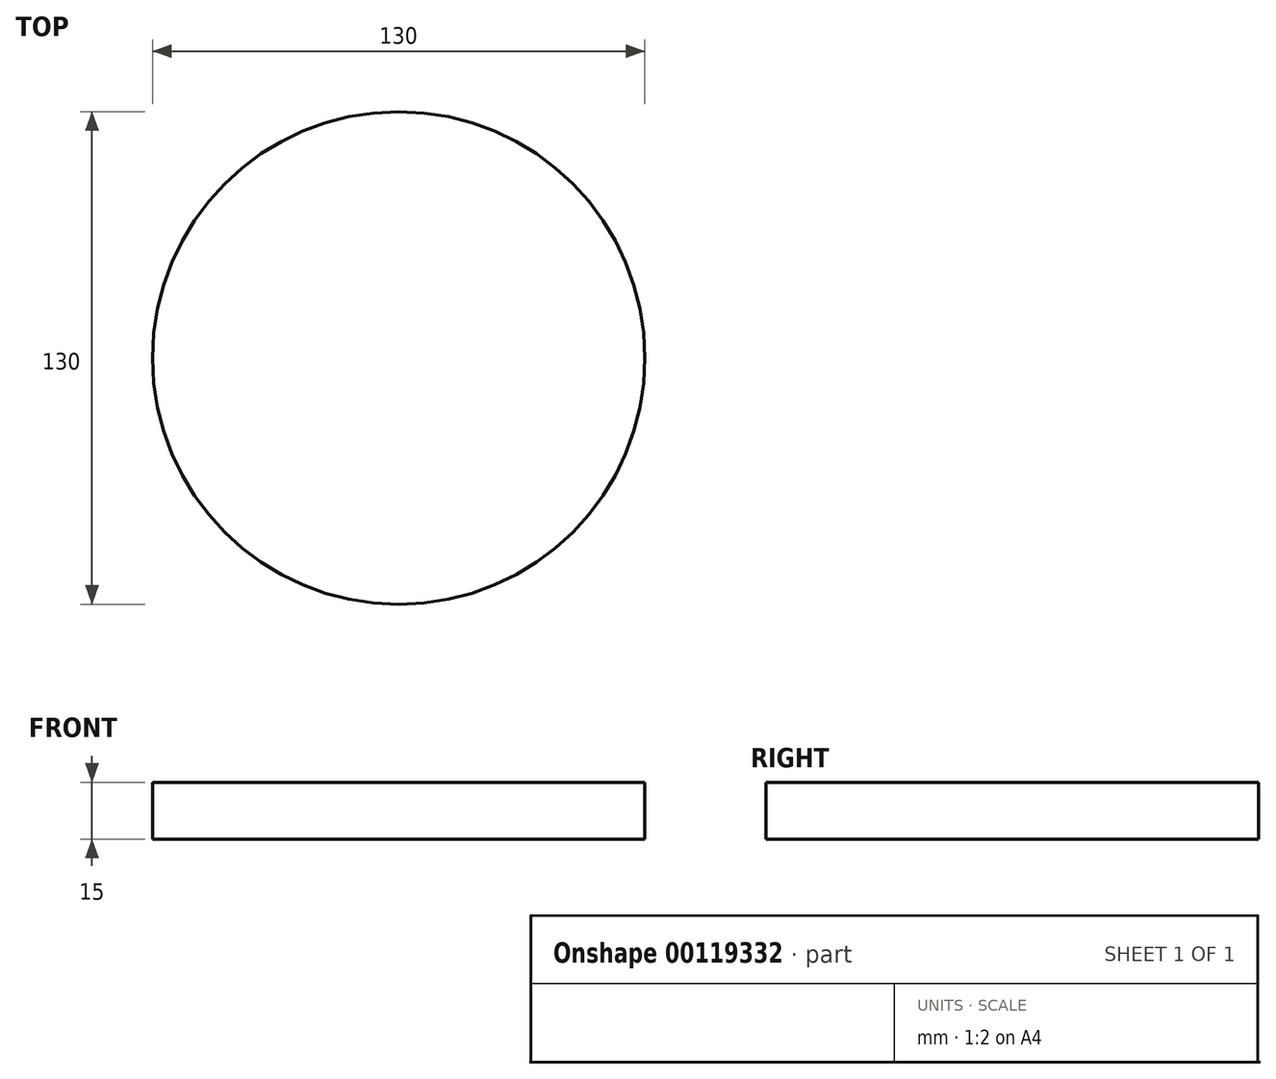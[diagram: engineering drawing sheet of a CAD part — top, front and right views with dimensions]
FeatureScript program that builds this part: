
annotation { "Feature Type Name" : "Feature", "Feature Type Description" : "" }
export const myFeature = defineFeature(function(context is Context, id is Id, definition is map)
    precondition{}
    {
        {
            var Q0;
            Q0=qCreatedBy(makeId("Top.planeOp"),FACE);
            var sketch = newSketch(context, id + "F0", { "sketchPlane" : qUnion([Q0])});
            skCircle(sketch, "E0", {"center": v(-98.16, 12.5) * mm, "radius": 65 * mm});
            skSolve(sketch);
        }
        {
            var Q0;
            Q0=makeQuery(id+"F0.imprint","IMPRINT",FACE,{"disambiguationData":[TD([[makeQuery(id+"F0.imprint","IMPRINT",EDGE,{"derivedFrom":sQuery(id+"F0.wireOp",EDGE,"E0")}),1.0]])]});
            extrude(context, id + "F1", {"entities" : qUnion([Q0]), "depth" : 15 * mm});
        }
    });
